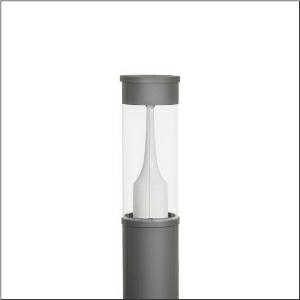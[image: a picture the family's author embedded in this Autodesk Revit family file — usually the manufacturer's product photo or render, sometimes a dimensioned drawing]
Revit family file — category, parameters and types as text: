
# Revit family: city-light_120_iq___p1_0a_5xa5285bf14h_8c15
name_source: partatom
category: Lighting Fixtures
units: mm (PartAtom-declared; Revit-internal decimal feet)

## family parameters
Cut with Voids When Loaded = No
Host = Face
Light Source = No
Part Type = Normal
Room Calculation Point = No
Round Connector Dimension = Use Diameter
Shared = No

## types (1)
- --- (1 x LED, 1510 lm, 12.9 W, 2200K)
    Apparent Load = 13 VA
    CIE Flux Codes = 32 61 90 93 100
    Color Rendering = 70
    Color Temperature = 2200K
    Default Elevation = 1800 mm
    Description = City-Light 120 iQ, bollard luminaire, Module 540 iQ-SR, primary light control with 3 zone facetted reflector, of plastic, silver coated, highly specular, structured, primary optical cover: cover, of PMMA, transparent, partly coated, light distribution: P1.0a, primary light characteristic: strongly asymmetric, LED, High Power LED, rated luminous flux: 1.510lm, luminous efficacy: 117lm/W, light colour: 722, colour temperature: 2200K, control gear: ECG iQ, control: presetting dimming logarithmic, Street-Remote, Auto-Match, Temp-Guard, Lumen-Switch, Night-Set, Smart-Wire, Light-Fading, Desk-Remote (wireless, voltage-free reading and setting of iQ features in the workshop via application-optimized NFC function/RFID function), optimised constant luminous flux control (CLO 2.0), with terminal, 6-pole, max. 2.5mm², mains connection: 220..240V, AC, 50/60Hz, start of lifetime: 13W, end of lifetime: 13W, reduction: 6W, luminaire housing, cylindrical, of extruded aluminium section, coated, Siteco® metallic grey (DB 702S), length: 1.200mm, diameter: 200mm, Module 540 iQ-SR, traffic white (RAL 9016), equipment: standard, protection rating (complete): IP54, insulation class (complete): insulation class II (safety insulation), certification: CE, ENEC, VDE, packaging unit: 1 piece

Light Distribution: P1.0a
    Height = 500 mm
    Lamp = 1 x LED
    Lamp Light Flux = 1510 lm
    Lamp Power = 12.9 W
    Lamp count = 1
    Length = 200 mm  [stored 0.656168 ft]
    Luminous efficacy = 117 lm/W
    Manufacturer = Siteco
    ModVariant = No
    Model = 5XA5285BF14H
    Number of Poles = 1
    OnlyDefault = Yes
    Power Factor = 1
    Product Name = City-Light 120 iQ | P1.0a
    Product group = bollard luminaire | pylon top
    ProductGroupID = 6104
    Protection Class = Protection class II
    Protection Degree = IP 54
    RLX_Detail_Level = 1
    RlxData = <blob elided: 52853 chars, md5=bbc9ce54>
    Socket = socket
    Standby Power = 0 W
    System Light Flux = 1510 lm
    System Power = 13 W
    Type Comments = factory setting: luminous flux: 100 % | dim-lin: 254 | 516 mA
    Type Image = l_1006922.jpg
    URL = http://relux.com
    VarID = @adj_070873
    Voltage = 0 V
    Weight = 0.00 kg
    Width = 0 mm  [stored 0 ft]

note: [stored X ft] marks values corroborated as IEEE doubles in the binary element streams (Revit-internal decimal feet)

## geometry (parser evidence)
native form markers: Blend x4, Sweep x12
no freeform markers — native parametric forms only
